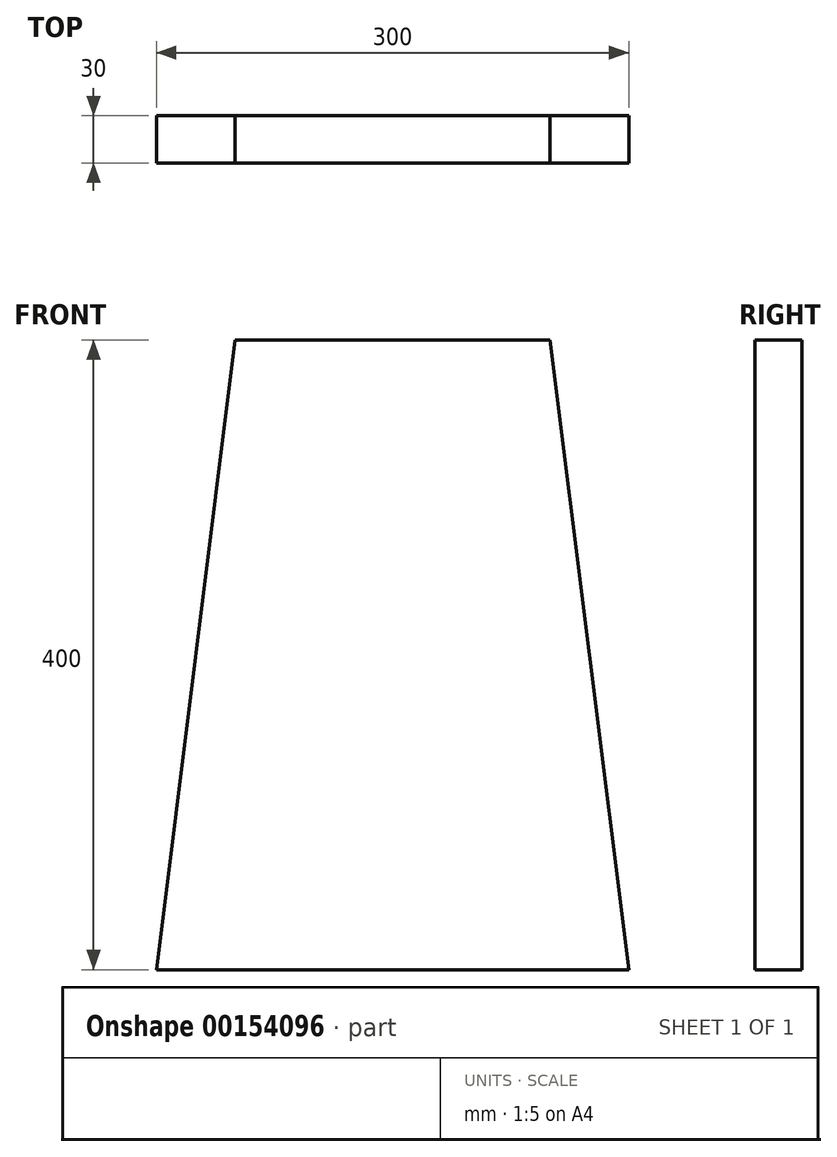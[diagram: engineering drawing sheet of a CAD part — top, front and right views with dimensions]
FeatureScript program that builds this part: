
annotation { "Feature Type Name" : "Feature", "Feature Type Description" : "" }
export const myFeature = defineFeature(function(context is Context, id is Id, definition is map)
    precondition{}
    {
        {
            var Q0;
            Q0=qCreatedBy(makeId("Top.planeOp"),FACE);
            var sketch = newSketch(context, id + "F0", { "sketchPlane" : qUnion([Q0])});
            skLineSegment(sketch, "E0.bottom", {"start": v(150, 15) * mm, "end": v(-150, 15) * mm});
            skLineSegment(sketch, "E0.top", {"start": v(150, -15) * mm, "end": v(-150, -15) * mm});
            skLineSegment(sketch, "E0.left", {"start": v(150, 15) * mm, "end": v(150, -15) * mm});
            skLineSegment(sketch, "E0.right", {"start": v(-150, 15) * mm, "end": v(-150, -15) * mm});
            skPoint(sketch, "E0.middle", {"position": v(0, 0) * mm});
            skSolve(sketch);
        }
        {
            var Q0;
            Q0=qCreatedBy(makeId("Top.planeOp"),FACE);
            cPlane(context, id + "F1", {"entities" : qUnion([Q0]), "cplaneType" : CPlaneType.OFFSET, "offset" : 400 * mm, "width" : 150 * mm, "height" : 150 * mm});
        }
        {
            var Q0;
            Q0=qCreatedBy(id+"F1.planeOp",FACE);
            var sketch = newSketch(context, id + "F2", { "sketchPlane" : qUnion([Q0])});
            skLineSegment(sketch, "E1.bottom", {"start": v(-100, 15) * mm, "end": v(100, 15) * mm});
            skLineSegment(sketch, "E1.top", {"start": v(-100, -15) * mm, "end": v(100, -15) * mm});
            skLineSegment(sketch, "E1.left", {"start": v(-100, 15) * mm, "end": v(-100, -15) * mm});
            skLineSegment(sketch, "E1.right", {"start": v(100, 15) * mm, "end": v(100, -15) * mm});
            skPoint(sketch, "E1.middle", {"position": v(0, 0) * mm});
            skSolve(sketch);
        }
        {
            var Q0;
            Q0=makeQuery(id+"F2.imprint","IMPRINT",FACE,{"disambiguationData":[TD([[makeQuery(id+"F2.imprint","IMPRINT",EDGE,{"derivedFrom":sQuery(id+"F2.wireOp",EDGE,"E1.bottom")}),-1.0]])]});
            var Q1;
            Q1=makeQuery(id+"F0.imprint","IMPRINT",FACE,{"disambiguationData":[TD([[makeQuery(id+"F0.imprint","IMPRINT",EDGE,{"derivedFrom":sQuery(id+"F0.wireOp",EDGE,"E0.bottom")}),1.0]])]});
            loft(context, id + "F3", {"sheetProfilesArray" : [{ "sheetProfileEntities" : qUnion([Q0]) }, { "sheetProfileEntities" : qUnion([Q1]) }]});
        }
    });
